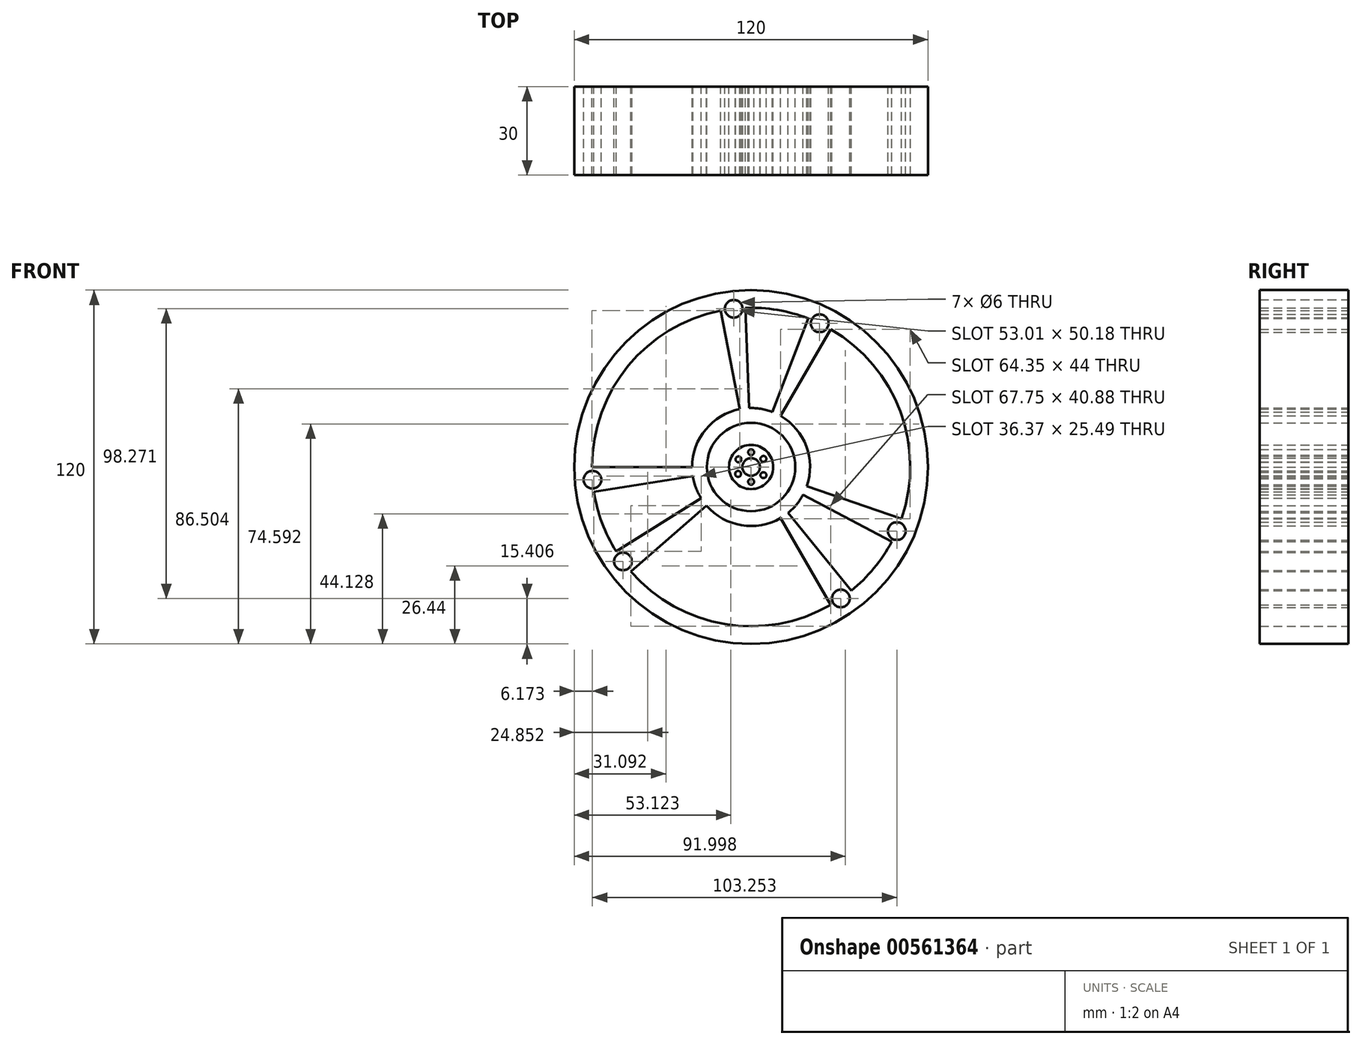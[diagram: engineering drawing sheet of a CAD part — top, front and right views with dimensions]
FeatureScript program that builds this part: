
annotation { "Feature Type Name" : "Feature", "Feature Type Description" : "" }
export const myFeature = defineFeature(function(context is Context, id is Id, definition is map)
    precondition{}
    {
        {
            var Q0;
            Q0=qCreatedBy(makeId("Front.planeOp"),FACE);
            var sketch = newSketch(context, id + "F0", { "sketchPlane" : qUnion([Q0])});
            skCircle(sketch, "E0", {"center": v(0, 0) * mm, "radius": 60 * mm});
            skCircle(sketch, "E1", {"center": v(0, 0) * mm, "radius": 54 * mm});
            skCircle(sketch, "E2", {"center": v(0, 0) * mm, "radius": 20 * mm});
            skCircle(sketch, "E3", {"center": v(0, 0) * mm, "radius": 15 * mm});
            skCircle(sketch, "E4", {"center": v(0, 0) * mm, "radius": 3 * mm});
            skLineSegment(sketch, "E5", {"start": v(-1.88, 53.97) * mm, "end": v(-0.7, 19.99) * mm});
            skLineSegment(sketch, "E6", {"start": v(19.35, 50.41) * mm, "end": v(7.17, 18.67) * mm});
            skLineSegment(sketch, "E7", {"start": v(-3.82, 19.63) * mm, "end": v(-10.3, 53) * mm});
            skLineSegment(sketch, "E8", {"start": v(10, 17.32) * mm, "end": v(27, 46.77) * mm});
            skLineSegment(sketch, "E9", {"start": v(18.91, -6.51) * mm, "end": v(51.06, -17.58) * mm});
            skLineSegment(sketch, "E10", {"start": v(17.66, -9.39) * mm, "end": v(47.68, -25.35) * mm});
            skLineSegment(sketch, "E11", {"start": v(12.59, -15.54) * mm, "end": v(33.98, -41.97) * mm});
            skLineSegment(sketch, "E12", {"start": v(10, -17.32) * mm, "end": v(27, -46.77) * mm});
            skLineSegment(sketch, "E13", {"start": v(-16.96, -10.6) * mm, "end": v(-45.8, -28.62) * mm});
            skLineSegment(sketch, "E14", {"start": v(-15.1, -13.12) * mm, "end": v(-40.75, -35.43) * mm});
            skLineSegment(sketch, "E15", {"start": v(-19.75, -3.13) * mm, "end": v(-53.34, -8.45) * mm});
            skLineSegment(sketch, "E16", {"start": v(-20, 0) * mm, "end": v(-54, 0) * mm});
            skCircle(sketch, "E17", {"center": v(-5.9, 53.68) * mm, "radius": 3 * mm});
            skCircle(sketch, "E18", {"center": v(23.25, 48.74) * mm, "radius": 3 * mm});
            skCircle(sketch, "E19", {"center": v(49.43, -21.75) * mm, "radius": 3 * mm});
            skCircle(sketch, "E20", {"center": v(30.45, -44.6) * mm, "radius": 3 * mm});
            skCircle(sketch, "E21", {"center": v(-43.47, -32.03) * mm, "radius": 3 * mm});
            skCircle(sketch, "E22", {"center": v(-53.83, -4.32) * mm, "radius": 3 * mm});
            skCircle(sketch, "E23", {"center": v(0, 0) * mm, "radius": 7.5 * mm});
            skCircle(sketch, "E24", {"center": v(0, 0) * mm, "radius": 5 * mm});
            skCircle(sketch, "E25", {"center": v(0, 0) * mm, "radius": 2 * mm});
            skCircle(sketch, "E26", {"center": v(0, 5) * mm, "radius": 1 * mm});
            skCircle(sketch, "E27", {"center": v(0, -5) * mm, "radius": 1 * mm});
            skCircle(sketch, "E28", {"center": v(4.16, -2.77) * mm, "radius": 1 * mm});
            skCircle(sketch, "E29", {"center": v(4.18, 2.75) * mm, "radius": 1 * mm});
            skCircle(sketch, "E30", {"center": v(-4.42, -2.35) * mm, "radius": 1 * mm});
            skCircle(sketch, "E31", {"center": v(-4.27, 2.6) * mm, "radius": 1 * mm});
            skSolve(sketch);
        }
        {
            var Q0;
            Q0 = qSketchRegion(id + "F0", true);
            var Q1;
            {var subQ0=sQuery(id+"F0.wireOp",EDGE,"E15");Q1=makeQuery(id+"F0.imprint","IMPRINT",FACE,{"disambiguationData":[TD([[makeQuery(id+"F0.imprint","IMPRINT",EDGE,{"derivedFrom":subQ0}),-1.0]])]});}
            var Q2;
            {var subQ0=sQuery(id+"F0.wireOp",EDGE,"E13");Q2=makeQuery(id+"F0.imprint","IMPRINT",FACE,{"disambiguationData":[TD([[makeQuery(id+"F0.imprint","IMPRINT",EDGE,{"derivedFrom":subQ0}),1.0]])]});}
            var Q3;
            {var subQ0=sQuery(id+"F0.wireOp",EDGE,"E11");Q3=makeQuery(id+"F0.imprint","IMPRINT",FACE,{"disambiguationData":[TD([[makeQuery(id+"F0.imprint","IMPRINT",EDGE,{"derivedFrom":subQ0}),-1.0]])]});}
            var Q4;
            {var subQ0=sQuery(id+"F0.wireOp",EDGE,"E9");Q4=makeQuery(id+"F0.imprint","IMPRINT",FACE,{"disambiguationData":[TD([[makeQuery(id+"F0.imprint","IMPRINT",EDGE,{"derivedFrom":subQ0}),-1.0]])]});}
            var Q5;
            {var subQ0=sQuery(id+"F0.wireOp",EDGE,"E6");Q5=makeQuery(id+"F0.imprint","IMPRINT",FACE,{"disambiguationData":[TD([[makeQuery(id+"F0.imprint","IMPRINT",EDGE,{"derivedFrom":subQ0}),1.0]])]});}
            var Q6;
            {var subQ0=sQuery(id+"F0.wireOp",EDGE,"E5");Q6=makeQuery(id+"F0.imprint","IMPRINT",FACE,{"disambiguationData":[TD([[makeQuery(id+"F0.imprint","IMPRINT",EDGE,{"derivedFrom":subQ0}),-1.0]])]});}
            var Q7;
            Q7=makeQuery(id+"F0.imprint","IMPRINT",FACE,{"disambiguationData":[TD([[makeQuery(id+"F0.imprint","IMPRINT",EDGE,{"derivedFrom":sQuery(id+"F0.wireOp",EDGE,"E3")}),-1.0]])]});
            var Q8;
            Q8=makeQuery(id+"F0.imprint","IMPRINT",FACE,{"disambiguationData":[TD([[makeQuery(id+"F0.imprint","IMPRINT",EDGE,{"derivedFrom":sQuery(id+"F0.wireOp",EDGE,"E23")}),1.0]])]});
            var Q9;
            Q9=makeQuery(id+"F0.imprint","IMPRINT",FACE,{"disambiguationData":[TD([[makeQuery(id+"F0.imprint","IMPRINT",EDGE,{"derivedFrom":sQuery(id+"F0.wireOp",EDGE,"E4")}),-1.0]])]});
            extrude(context, id + "F1", {"entities" : qUnion([Q0, Q1, Q2, Q3, Q4, Q5, Q6, Q7, Q8, Q9]), "depth" : 30 * mm, "offsetDistance" : 25 * mm});
        }
    });
